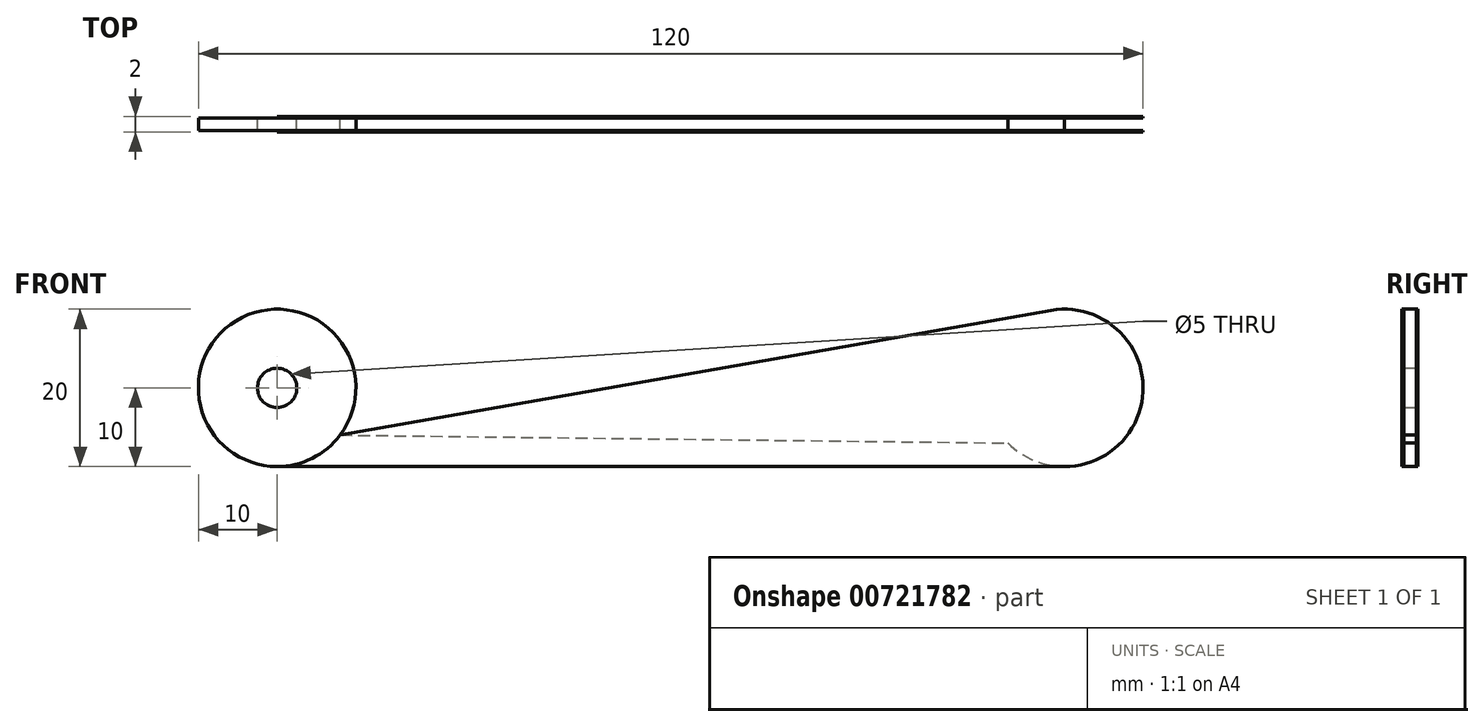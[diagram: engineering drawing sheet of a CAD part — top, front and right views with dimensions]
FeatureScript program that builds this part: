
annotation { "Feature Type Name" : "Feature", "Feature Type Description" : "" }
export const myFeature = defineFeature(function(context is Context, id is Id, definition is map)
    precondition{}
    {
        {
            assignVariable(context, id + "F0", {"name" : "t1", "anyValue" : 0.2});
        }
        {
            assignVariable(context, id + "F1", {"name" : "T1", "anyValue" : 2});
        }
        {
            var Q0;
            Q0=qCreatedBy(makeId("Front.planeOp"),FACE);
            var sketch = newSketch(context, id + "F2", { "sketchPlane" : qUnion([Q0])});
            skLineSegment(sketch, "E0", {"start": v(0, 0) * mm, "end": v(100, 0) * mm});
            skArc(sketch, "E1", {"start": v(100, 0) * mm, "mid": v(109.96, 10.87) * mm, "end": v(98.27, 19.85) * mm});
            skLineSegment(sketch, "E2", {"start": v(8, 4) * mm, "end": v(98.27, 19.85) * mm});
            skArc(sketch, "E3", {"start": v(0, 0) * mm, "mid": v(4.47, 1.06) * mm, "end": v(8, 4) * mm});
            skSolve(sketch);
        }
        {
            var Q0;
            Q0 = qSketchRegion(id + "F2", true);
            extrude(context, id + "F3", {"entities" : qUnion([Q0]), "depth" : (getVariable(context, 'T1') / 2) * mm, "offsetDistance" : 25 * mm, "hasSecondDirection" : true, "secondDirectionOppositeDirection" : false, "secondDirectionDepth" : (getVariable(context, 'T1') / 2 - getVariable(context, 't1')) * mm});
        }
        {
            var Q0;
            Q0 = qSketchRegion(id + "F2", true);
            extrude(context, id + "F4", {"entities" : qUnion([Q0]), "operationType" : NewBodyOperationType.ADD, "oppositeDirection" : true, "depth" : (getVariable(context, 'T1') / 2) * mm, "offsetDistance" : 25 * mm, "hasSecondDirection" : true, "secondDirectionOppositeDirection" : true, "secondDirectionDepth" : (getVariable(context, 'T1') / 2 - getVariable(context, 't1')) * mm});
        }
        {
            var Q0;
            Q0=qCreatedBy(makeId("Front.planeOp"),FACE);
            var sketch = newSketch(context, id + "F5", { "sketchPlane" : qUnion([Q0])});
            skLineSegment(sketch, "E4", {"start": v(0, 0) * mm, "end": v(100, 0) * mm});
            skLineSegment(sketch, "E5", {"start": v(8, 4) * mm, "end": v(92.86, 3) * mm});
            skPoint(sketch, "E6", {"position": v(0, 10) * mm});
            skArc(sketch, "E7", {"start": v(8, 4) * mm, "mid": v(-4.47, 18.94) * mm, "end": v(0, 0) * mm});
            skArc(sketch, "E8", {"start": v(92.86, 3) * mm, "mid": v(96.13, 0.78) * mm, "end": v(100, 0) * mm});
            skCircle(sketch, "E9", {"center": v(0, 10) * mm, "radius": 2.5 * mm});
            skSolve(sketch);
        }
        {
            var Q0;
            Q0 = qSketchRegion(id + "F5", true);
            extrude(context, id + "F6", {"entities" : qUnion([Q0]), "operationType" : NewBodyOperationType.ADD, "endBound" : BoundingType.SYMMETRIC, "depth" : (getVariable(context, 'T1') - 2 * getVariable(context, 't1')) * mm, "offsetDistance" : 25 * mm});
        }
    });
